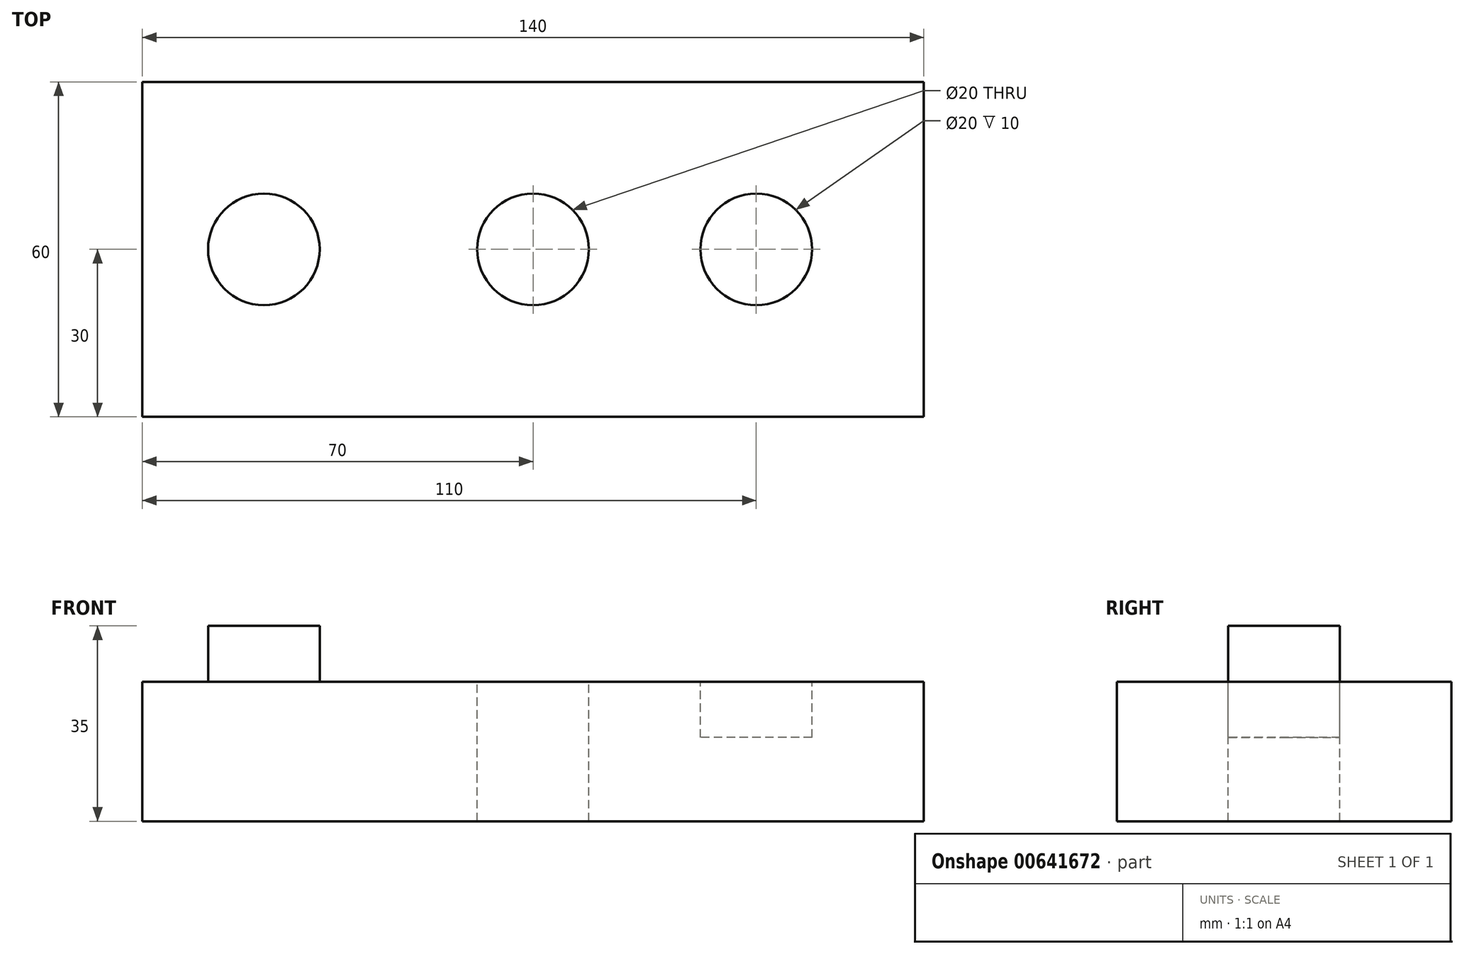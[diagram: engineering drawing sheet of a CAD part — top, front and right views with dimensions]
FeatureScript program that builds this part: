
annotation { "Feature Type Name" : "Feature", "Feature Type Description" : "" }
export const myFeature = defineFeature(function(context is Context, id is Id, definition is map)
    precondition{}
    {
        {
            var Q0;
            Q0=qCreatedBy(makeId("Top.planeOp"),FACE);
            var sketch = newSketch(context, id + "F0", { "sketchPlane" : qUnion([Q0])});
            skLineSegment(sketch, "E0.bottom", {"start": v(-70, 30) * mm, "end": v(70, 30) * mm});
            skLineSegment(sketch, "E0.top", {"start": v(-70, -30) * mm, "end": v(70, -30) * mm});
            skLineSegment(sketch, "E0.left", {"start": v(-70, 30) * mm, "end": v(-70, -30) * mm});
            skLineSegment(sketch, "E0.right", {"start": v(70, 30) * mm, "end": v(70, -30) * mm});
            skPoint(sketch, "E0.middle", {"position": v(0, 0) * mm});
            skSolve(sketch);
        }
        {
            var Q0;
            Q0=makeQuery(id+"F0.imprint","IMPRINT",FACE,{"disambiguationData":[TD([[makeQuery(id+"F0.imprint","IMPRINT",EDGE,{"derivedFrom":sQuery(id+"F0.wireOp",EDGE,"E0.bottom")}),-1.0]])]});
            extrude(context, id + "F1", {"entities" : qUnion([Q0]), "depth" : 25 * mm, "offsetDistance" : 25 * mm});
        }
        {
            var Q0;
            Q0=makeQuery(id+"F1.opExtrude","CAP_FACE",FACE,{"disambiguationData":[OSD([sQuery(id+"F0.wireOp",EDGE,"E0.bottom"),sQuery(id+"F0.wireOp",EDGE,"E0.top"),sQuery(id+"F0.wireOp",EDGE,"E0.left"),sQuery(id+"F0.wireOp",EDGE,"E0.right")])],"isStart":false});
            var sketch = newSketch(context, id + "F2", { "sketchPlane" : qUnion([Q0])});
            skCircle(sketch, "E1", {"center": v(-48.22, 0) * mm, "radius": 10 * mm});
            skSolve(sketch);
        }
        {
            var Q0;
            Q0=makeQuery(id+"F2.imprint","IMPRINT",FACE,{"disambiguationData":[TD([[makeQuery(id+"F2.imprint","IMPRINT",EDGE,{"derivedFrom":sQuery(id+"F2.wireOp",EDGE,"E1")}),-1.0]])]});
            var sketch = newSketch(context, id + "F3", { "sketchPlane" : qUnion([Q0])});
            skCircle(sketch, "E2", {"center": v(40, 0) * mm, "radius": 10 * mm});
            skSolve(sketch);
        }
        {
            var Q0;
            Q0=makeQuery(id+"F2.imprint","IMPRINT",FACE,{"disambiguationData":[TD([[makeQuery(id+"F2.imprint","IMPRINT",EDGE,{"derivedFrom":sQuery(id+"F2.wireOp",EDGE,"E1")}),-1.0]])]});
            var sketch = newSketch(context, id + "F4", { "sketchPlane" : qUnion([Q0])});
            skCircle(sketch, "E3", {"center": v(0, 0) * mm, "radius": 10 * mm});
            skSolve(sketch);
        }
        {
            var Q0;
            Q0 = qSketchRegion(id + "F2", true);
            extrude(context, id + "F5", {"entities" : qUnion([Q0]), "operationType" : NewBodyOperationType.ADD, "depth" : 10 * mm, "offsetDistance" : 25 * mm});
        }
        {
            var Q0;
            Q0 = qSketchRegion(id + "F4", true);
            extrude(context, id + "F6", {"entities" : qUnion([Q0]), "operationType" : NewBodyOperationType.REMOVE, "oppositeDirection" : true, "depth" : 41.8 * mm, "offsetDistance" : 25 * mm});
        }
        {
            var Q0;
            Q0 = qSketchRegion(id + "F3", true);
            extrude(context, id + "F7", {"entities" : qUnion([Q0]), "operationType" : NewBodyOperationType.REMOVE, "oppositeDirection" : true, "depth" : 10 * mm, "offsetDistance" : 25 * mm});
        }
    });
